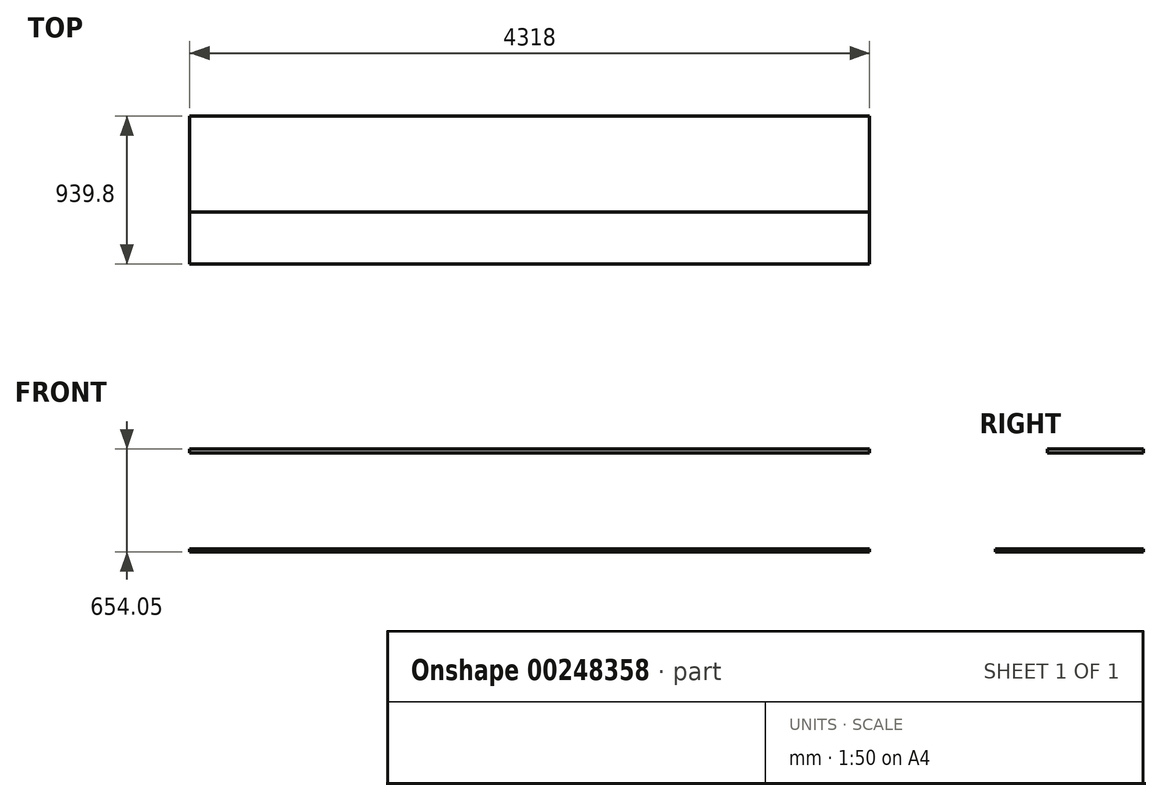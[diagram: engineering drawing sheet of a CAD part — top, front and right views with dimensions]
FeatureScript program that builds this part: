
annotation { "Feature Type Name" : "Feature", "Feature Type Description" : "" }
export const myFeature = defineFeature(function(context is Context, id is Id, definition is map)
    precondition{}
    {
        {
            var Q0;
            Q0=qCreatedBy(makeId("Top.planeOp"),FACE);
            var sketch = newSketch(context, id + "F0", { "sketchPlane" : qUnion([Q0])});
            skLineSegment(sketch, "E0.bottom", {"start": v(2159, -469.9) * mm, "end": v(-2159, -469.9) * mm});
            skLineSegment(sketch, "E0.top", {"start": v(2159, 469.9) * mm, "end": v(-2159, 469.9) * mm});
            skLineSegment(sketch, "E0.left", {"start": v(2159, -469.9) * mm, "end": v(2159, 469.9) * mm});
            skLineSegment(sketch, "E0.right", {"start": v(-2159, -469.9) * mm, "end": v(-2159, 469.9) * mm});
            skPoint(sketch, "E0.middle", {"position": v(0, 0) * mm});
            skSolve(sketch);
        }
        {
            var Q0;
            Q0=makeQuery(id+"F0.imprint","IMPRINT",FACE,{"disambiguationData":[TD([[makeQuery(id+"F0.imprint","IMPRINT",EDGE,{"derivedFrom":sQuery(id+"F0.wireOp",EDGE,"E0.bottom")}),-1.0]])]});
            extrude(context, id + "F1", {"entities" : qUnion([Q0]), "depth" : 19.05 * mm});
        }
        {
            var Q0;
            Q0=makeQuery(id+"F1.opExtrude","CAP_FACE",FACE,{"disambiguationData":[OSD([sQuery(id+"F0.wireOp",EDGE,"E0.bottom"),sQuery(id+"F0.wireOp",EDGE,"E0.top"),sQuery(id+"F0.wireOp",EDGE,"E0.left"),sQuery(id+"F0.wireOp",EDGE,"E0.right")])],"isStart":true});
            var sketch = newSketch(context, id + "F2", { "sketchPlane" : qUnion([Q0])});
            skLineSegment(sketch, "E1", {"start": v(-2159, 469.9) * mm, "end": v(-2159, -469.9) * mm});
            skLineSegment(sketch, "E2", {"start": v(2159, 469.9) * mm, "end": v(2159, -469.9) * mm});
            skLineSegment(sketch, "E3", {"start": v(-637.29, 469.9) * mm, "end": v(-637.29, -469.9) * mm});
            skLineSegment(sketch, "E4", {"start": v(250.41, 469.9) * mm, "end": v(250.41, -469.9) * mm});
            skSolve(sketch);
        }
        {
            var Q0;
            Q0=makeQuery(id+"F1.opExtrude","CAP_FACE",FACE,{"disambiguationData":[OSD([sQuery(id+"F0.wireOp",EDGE,"E0.bottom"),sQuery(id+"F0.wireOp",EDGE,"E0.top"),sQuery(id+"F0.wireOp",EDGE,"E0.left"),sQuery(id+"F0.wireOp",EDGE,"E0.right")])],"isStart":false});
            cPlane(context, id + "F3", {"entities" : qUnion([Q0]), "cplaneType" : CPlaneType.OFFSET, "offset" : 609.6 * mm, "width" : 152.4 * mm, "height" : 152.4 * mm});
        }
        {
            var Q0;
            {var subQ0=sQuery(id+"F2.wireOp",EDGE,"E1");Q0=makeQuery(id+"F2.imprint","IMPRINT",FACE,{"disambiguationData":[TD([[makeQuery(id+"F2.imprint","IMPRINT",EDGE,{"derivedFrom":subQ0}),1.0]])]});}
            var Q1;
            Q1=sQuery(id+"F2.wireOp",EDGE,"E1");
            var Q2;
            Q2=sQuery(id+"F2.wireOp",EDGE,"E3");
            var Q3;
            Q3=sQuery(id+"F2.wireOp",EDGE,"E4");
            var Q4;
            Q4=sQuery(id+"F2.wireOp",EDGE,"E2");
            extrude(context, id + "F4", {"entities" : qUnion([Q0]), "bodyType" : ToolBodyType.SURFACE, "surfaceEntities" : qUnion([Q1, Q2, Q3, Q4]), "depth" : 889 * mm});
        }
        {
            var Q0;
            Q0=makeQuery(id+"F1.opExtrude","CAP_FACE",FACE,{"disambiguationData":[OSD([sQuery(id+"F0.wireOp",EDGE,"E0.bottom"),sQuery(id+"F0.wireOp",EDGE,"E0.top"),sQuery(id+"F0.wireOp",EDGE,"E0.left"),sQuery(id+"F0.wireOp",EDGE,"E0.right")])],"isStart":false});
            var sketch = newSketch(context, id + "F5", { "sketchPlane" : qUnion([Q0])});
            skLineSegment(sketch, "E5", {"start": v(-2159, 469.9) * mm, "end": v(-2159, -139.7) * mm});
            skLineSegment(sketch, "E6", {"start": v(-367, 469.9) * mm, "end": v(-367, -139.7) * mm});
            skLineSegment(sketch, "E7", {"start": v(205.36, 469.9) * mm, "end": v(205.36, -139.7) * mm});
            skLineSegment(sketch, "E8", {"start": v(2159, 469.9) * mm, "end": v(2159, -139.7) * mm});
            skSolve(sketch);
        }
        {
            var Q0;
            Q0 = qSketchRegion(id + "F5", true);
            var Q1;
            Q1 = qConstructionFilter(qBodyType(qCreatedBy(id + "F5" ,EDGE), BodyType.WIRE), ConstructionObject.NO);
            var Q2;
            Q2=qCreatedBy(id+"F3.planeOp",FACE);
            extrude(context, id + "F6", {"entities" : qUnion([Q0]), "bodyType" : ToolBodyType.SURFACE, "surfaceEntities" : qUnion([Q1]), "endBound" : BoundingType.UP_TO_SURFACE, "endBoundEntityFace" : qUnion([Q2]), "depth" : 635 * mm});
        }
        {
            var Q0;
            Q0=qCreatedBy(id+"F3.planeOp",FACE);
            var sketch = newSketch(context, id + "F7", { "sketchPlane" : qUnion([Q0])});
            skLineSegment(sketch, "E9.bottom", {"start": v(-2159, 469.9) * mm, "end": v(2159, 469.9) * mm});
            skLineSegment(sketch, "E9.top", {"start": v(-2159, -139.7) * mm, "end": v(2159, -139.7) * mm});
            skLineSegment(sketch, "E9.left", {"start": v(-2159, 469.9) * mm, "end": v(-2159, -139.7) * mm});
            skLineSegment(sketch, "E9.right", {"start": v(2159, 469.9) * mm, "end": v(2159, -139.7) * mm});
            skSolve(sketch);
        }
        {
            var Q0;
            Q0=makeQuery(id+"F7.imprint","IMPRINT",FACE,{"disambiguationData":[TD([[makeQuery(id+"F7.imprint","IMPRINT",EDGE,{"derivedFrom":sQuery(id+"F7.wireOp",EDGE,"E9.bottom")}),-1.0]])]});
            extrude(context, id + "F8", {"entities" : qUnion([Q0]), "depth" : 25.4 * mm});
        }
    });
